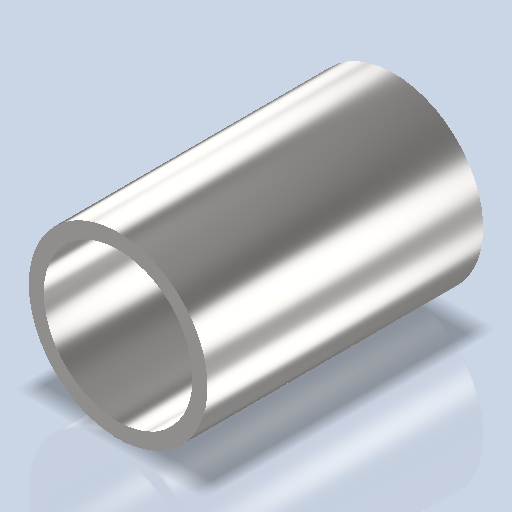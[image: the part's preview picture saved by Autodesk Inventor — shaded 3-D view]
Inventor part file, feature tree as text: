
AUTODESK INVENTOR PART (.ipt)
format: ipt  version: 2024 (Build 280153000, 153)  size: 216,576 bytes
history: native  units: mm
features: extrude x1, sketch x1
ambient origin geometry x8: Origin, YZ Plane, XZ Plane, XY Plane, X Axis, Y Axis, Z Axis, Center Point
bodies: Volumenkörper1 (feature_tree)
feature tree (2):
  extrude  "Extrusion1"  Depth=10.0mm
  sketch  "Skizze1"  dims[d0=12.0mm d1=10.0mm d2=18.5mm d3=0.0mm]
